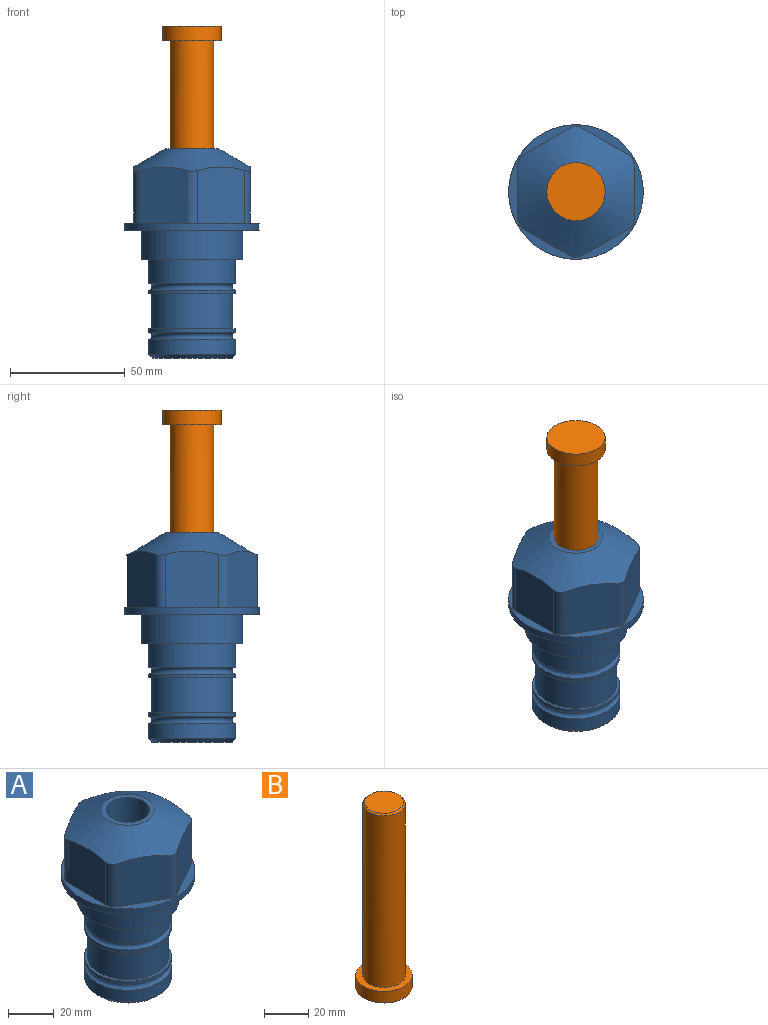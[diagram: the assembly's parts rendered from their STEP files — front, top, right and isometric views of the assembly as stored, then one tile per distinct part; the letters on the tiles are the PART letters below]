
ASSEMBLY  parts=2 mates=1
PART A: 36 faces, bbox 58.7x58.7x91.2 mm
  f0: cylinder r=17.78mm len=35.56mm, axis (0,0,1), area 1670.8mm2, adj f23,f24,f31
  f1: cylinder r=19.05mm len=38.1mm, axis (0,0,1), area 1191.9mm2, adj f26,f27,f30
  f2: plane 58.66x58.66mm, normal (0,0,-1), area 1150.6mm2, adj f3,f28
  f3: cylinder r=29.33mm len=58.66mm, axis (0,0,-1), area 585.1mm2, adj f2,f4
  f4: plane 58.66x58.66mm, normal (0,0,1), area 475.9mm2, adj f3,f5,f6,f7,f8,f9,f10,f11
  f5: plane 24.5x20.32mm, normal (-0.5,0.87,0), area 562.8mm2, adj f4,f15,f16,f17
  f6: plane 24.5x20.32mm, normal (0.5,0.87,0), area 562.8mm2, adj f4,f14,f15,f17
  f7: plane 24.5x23.48mm, normal (1,0,0), area 562.8mm2, adj f4,f13,f14,f17
  f8: plane 24.5x20.32mm, normal (0.5,-0.87,0), area 562.8mm2, adj f4,f12,f13,f17
  f9: plane 24.5x20.32mm, normal (-0.5,-0.87,0), area 562.8mm2, adj f4,f11,f12,f17
  f10: plane 24.5x23.48mm, normal (-1,0,0), area 562.8mm2, adj f4,f11,f16,f17
  f11: cylinder r=5.08mm len=23.01mm, axis (0,0,-1), area 121.2mm2, adj f4,f9,f10,f17
  f12: cylinder r=5.08mm len=23.01mm, axis (0,0,-1), area 121.2mm2, adj f4,f8,f9,f17
  f13: cylinder r=5.08mm len=23.01mm, axis (0,0,-1), area 121.2mm2, adj f4,f7,f8,f17
  f14: cylinder r=5.08mm len=23.01mm, axis (0,0,-1), area 121.2mm2, adj f4,f6,f7,f17
  f15: cylinder r=5.08mm len=23.01mm, axis (0,0,-1), area 121.2mm2, adj f4,f5,f6,f17
  f16: cylinder r=5.08mm len=23.01mm, axis (0,0,-1), area 121.2mm2, adj f4,f5,f10,f17
  f17: cone r=11.73mm half-angle=60deg, axis (0,0,-1), area 2071.8mm2, adj f5,f6,f7,f8,f9,f10,f11,f12
  f18: plane 23.46x23.46mm, normal (0,0,1), area 147.4mm2, adj f17,f35
  f19: plane 34.93x34.93mm, normal (0,0,-1), area 958mm2, adj f29
  f20: cylinder r=19.05mm len=38.1mm, axis (0,0,1), area 760.1mm2, adj f21,f29
  f21: torus R=19.05mm, axis (0,0,1), area 565.3mm2, adj f20,f22
  f22: cylinder r=19.05mm len=38.1mm, axis (0,0,1), area 190mm2, adj f21,f23
  f23: plane 38.1x38.1mm, normal (0,0,1), area 146.9mm2, adj f0,f22
  f24: plane 38.1x38.1mm, normal (0,0,-1), area 146.9mm2, adj f0,f25
  f25: cylinder r=19.05mm len=38.1mm, axis (0,0,1), area 190mm2, adj f24,f26
  f26: torus R=19.05mm, axis (0,0,1), area 565.3mm2, adj f1,f25
  f27: plane 44.45x44.45mm, normal (0,0,-1), area 411.7mm2, adj f1,f28
  f28: cylinder r=22.23mm len=44.45mm, axis (0,0,1), area 1773.5mm2, adj f2,f27
  f29: cone r=19.05mm half-angle=45deg, axis (0,0,1), area 257.5mm2, adj f19,f20
  f30: cylinder r=3.17mm len=6.75mm, axis (-1,0,0), area 128mm2, adj f1,f33
  f31: cylinder r=3.17mm len=6.35mm, axis (-1,0,0), area 102.5mm2, adj f0,f33
  f32: plane 25.4x25.4mm, normal (0,0,1), area 506.7mm2, adj f33
  f33: cylinder r=12.7mm len=66.42mm, axis (0,0,-1), area 5236.2mm2, adj f30,f31,f32,f34
  f34: cone r=9.53mm half-angle=30deg, axis (0,0,-1), area 443.4mm2, adj f33,f35
  f35: cylinder r=9.53mm len=19.05mm, axis (0,0,-1), area 849mm2, adj f18,f34
PART B: 6 faces, bbox 25.4x25.4x101.6 mm
  f0: plane 17.46x17.46mm, normal (0,0,1), area 239.5mm2, adj f5
  f1: plane 25.4x25.4mm, normal (0,0,-1), area 506.7mm2, adj f2
  f2: cylinder r=12.7mm len=25.4mm, axis (0,0,1), area 506.7mm2, adj f1,f3
  f3: plane 25.4x25.4mm, normal (0,0,1), area 221.7mm2, adj f2,f4
  f4: cylinder r=9.53mm len=94.46mm, axis (0,0,1), area 5653mm2, adj f3,f5
  f5: cone r=8.73mm half-angle=45deg, axis (0,0,-1), area 64.4mm2, adj f0,f4
PLACE A t=(11.1,-15.76,-18.13)mm
PLACE B rot(axis=(1,0,0),180deg) t=(11.1,-15.76,43.07)mm
MATE slider B.f2 <-> A.f0  axis (0,0,-1) through (11.1,-15.76,17.43)mm
